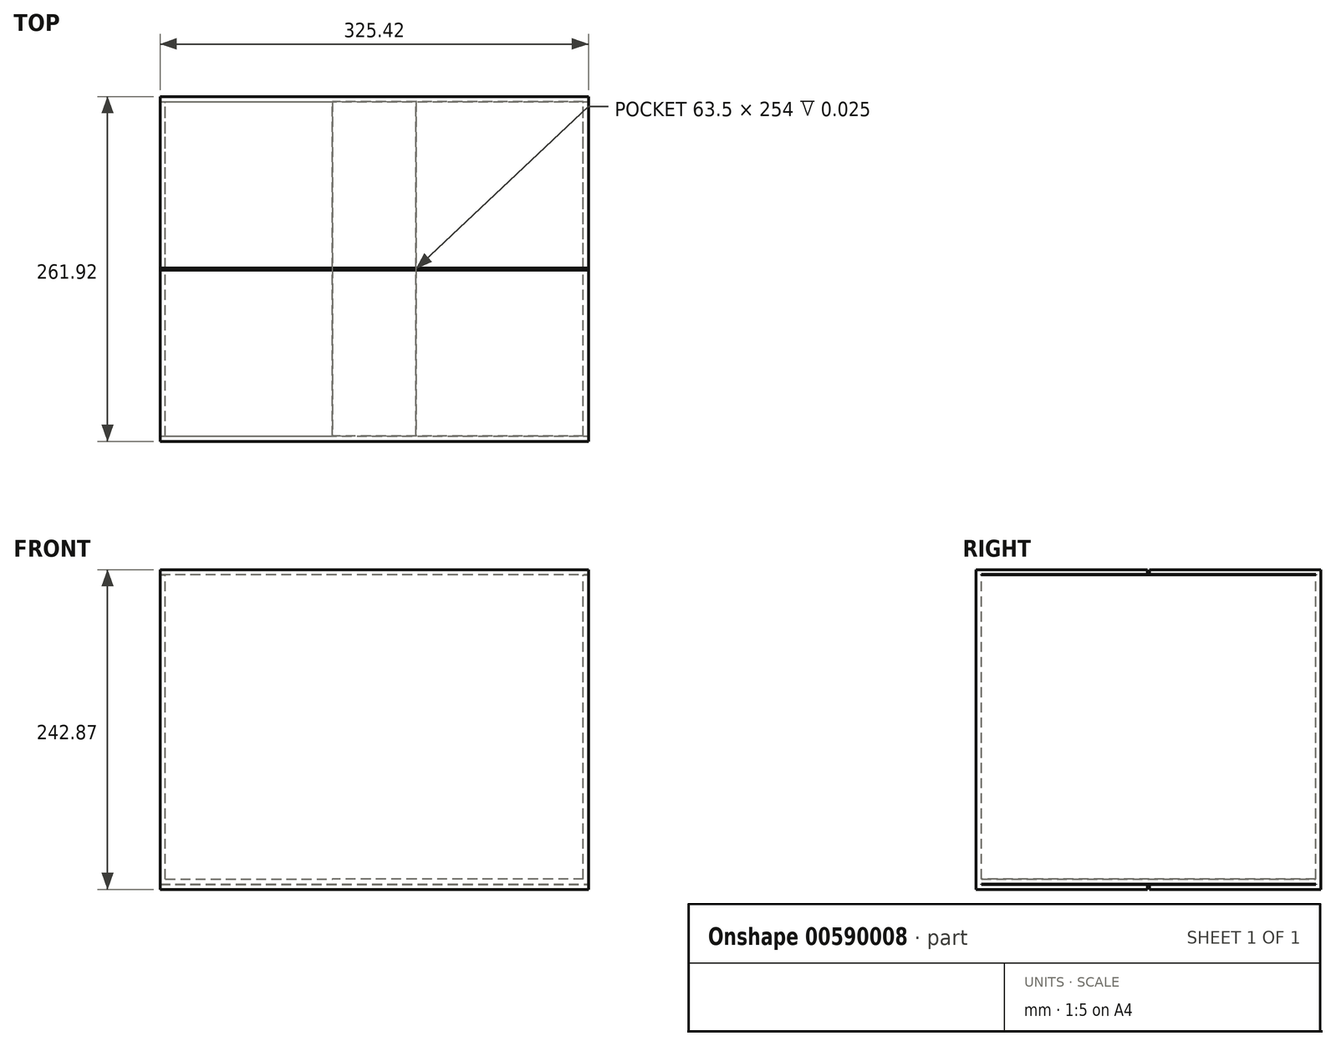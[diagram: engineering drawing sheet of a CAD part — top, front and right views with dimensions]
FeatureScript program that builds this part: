
annotation { "Feature Type Name" : "Feature", "Feature Type Description" : "" }
export const myFeature = defineFeature(function(context is Context, id is Id, definition is map)
    precondition{}
    {
        {
            var Q0;
            Q0=qCreatedBy(makeId("Top.planeOp"),FACE);
            var sketch = newSketch(context, id + "F0", { "sketchPlane" : qUnion([Q0])});
            skLineSegment(sketch, "E0.bottom", {"start": v(162.71, 130.96) * mm, "end": v(-162.71, 130.96) * mm});
            skLineSegment(sketch, "E0.top", {"start": v(162.71, -130.96) * mm, "end": v(-162.71, -130.96) * mm});
            skLineSegment(sketch, "E0.left", {"start": v(162.71, 130.96) * mm, "end": v(162.71, -130.96) * mm});
            skLineSegment(sketch, "E0.right", {"start": v(-162.71, 130.96) * mm, "end": v(-162.71, -130.96) * mm});
            skPoint(sketch, "E0.middle", {"position": v(0, 0) * mm});
            skSolve(sketch);
        }
        {
            var Q0;
            Q0 = qSketchRegion(id + "F0", true);
            extrude(context, id + "F1", {"entities" : qUnion([Q0]), "depth" : 242.87 * mm, "offsetDistance" : 25.4 * mm});
        }
        {
            var Q0;
            Q0=makeQuery(id+"F1.opExtrude","CAP_FACE",FACE,{"disambiguationData":[OSD([sQuery(id+"F0.wireOp",EDGE,"E0.bottom"),sQuery(id+"F0.wireOp",EDGE,"E0.top"),sQuery(id+"F0.wireOp",EDGE,"E0.left"),sQuery(id+"F0.wireOp",EDGE,"E0.right")])],"isStart":false});
            var sketch = newSketch(context, id + "F2", { "sketchPlane" : qUnion([Q0])});
            skLineSegment(sketch, "E1.bottom", {"start": v(158.75, 127) * mm, "end": v(-158.75, 127) * mm});
            skLineSegment(sketch, "E1.top", {"start": v(158.75, -127) * mm, "end": v(-158.75, -127) * mm});
            skLineSegment(sketch, "E1.left", {"start": v(158.75, 127) * mm, "end": v(158.75, -127) * mm});
            skLineSegment(sketch, "E1.right", {"start": v(-158.75, 127) * mm, "end": v(-158.75, -127) * mm});
            skPoint(sketch, "E1.middle", {"position": v(0, 0) * mm});
            skSolve(sketch);
        }
        {
            var Q0;
            Q0 = qSketchRegion(id + "F2", true);
            extrude(context, id + "F3", {"entities" : qUnion([Q0]), "operationType" : NewBodyOperationType.REMOVE, "oppositeDirection" : true, "depth" : 234.95 * mm, "offsetDistance" : 25.4 * mm});
        }
        {
            var Q0;
            Q0=makeQuery(id+"FU8CDPnAfcsiamF_1.boolean.opBoolean","MERGE",FACE,{"derivedFrom":[makeQuery(id+"FkqQ1I0agcOGDgH_1.boolean.opBoolean","MERGE",FACE,{"derivedFrom":[makeQuery(id+"F1.opExtrude","SWEPT_FACE",FACE,{"disambiguationData":[OSD([sQuery(id+"F0.wireOp",EDGE,"E0.left")])]}),makeQuery(id+"FkqQ1I0agcOGDgH_1.opExtrude","CAP_FACE",FACE,{"disambiguationData":[OSD([sQuery(id+"FoDB1Ja4WnMUcBU_1.wireOp",EDGE,"G9ktgCgW-cgai-Fx6D-LfIr-onLoDjvsxL8P"),sQuery(id+"FoDB1Ja4WnMUcBU_1.wireOp",EDGE,"sdlmHgrP-dK7O-7TKQ-vJt8-3tbjKW43ichT"),sQuery(id+"FoDB1Ja4WnMUcBU_1.wireOp",EDGE,"px5y0XHo-arw6-IYJl-GCBX-8e45FcqrlFcx"),sQuery(id+"FoDB1Ja4WnMUcBU_1.wireOp",EDGE,"WPK3Supz-hSMR-a29S-F5kb-zUsID9ybsl2w")])],"isStart":true})]}),makeQuery(id+"FU8CDPnAfcsiamF_1.opExtrude","CAP_FACE",FACE,{"disambiguationData":[OSD([sQuery(id+"Fmsg3vMfZlMDxUX_1.wireOp",EDGE,"k8SHwNhE-juRS-rYz1-FTam-3ZzICyqcjuc2"),sQuery(id+"Fmsg3vMfZlMDxUX_1.wireOp",EDGE,"0DMKhqTQ-7xsP-FRrA-W66T-bKl7aLMX0dlD"),sQuery(id+"Fmsg3vMfZlMDxUX_1.wireOp",EDGE,"qFIxm7PK-wiqi-QzEb-MUsV-y8MnjfuZhfVg"),sQuery(id+"Fmsg3vMfZlMDxUX_1.wireOp",EDGE,"azvGMKYQ-cPQm-AWe1-ROgs-fUFS8ZqJpbH7")])],"isStart":true})]});
            var sketch = newSketch(context, id + "F4", { "sketchPlane" : qUnion([Q0])});
            skLineSegment(sketch, "E2.bottom", {"start": v(0.8, 3.96) * mm, "end": v(-0.8, 3.96) * mm});
            skLineSegment(sketch, "E2.top", {"start": v(0.8, -3.96) * mm, "end": v(-0.8, -3.96) * mm});
            skLineSegment(sketch, "E2.left", {"start": v(0.8, 3.58) * mm, "end": v(0.8, -3.96) * mm});
            skLineSegment(sketch, "E2.right", {"start": v(-0.8, 3.58) * mm, "end": v(-0.8, -3.96) * mm});
            skPoint(sketch, "E2.middle", {"position": v(0, 0) * mm});
            skLineSegment(sketch, "E3.bottom", {"start": v(-0.8, 3.96) * mm, "end": v(-127, 3.96) * mm});
            skLineSegment(sketch, "E3.top", {"start": v(-0.8, 3.58) * mm, "end": v(-127, 3.58) * mm});
            skLineSegment(sketch, "E3.right", {"start": v(-127, 3.96) * mm, "end": v(-127, 3.58) * mm});
            skLineSegment(sketch, "E4", {"start": v(0, 0) * mm, "end": v(0, 24.77) * mm, "construction": true});
            skLineSegment(sketch, "E5.MirrorCS", {"start": v(127, 3.96) * mm, "end": v(127, 3.58) * mm});
            skLineSegment(sketch, "E6.MirrorCS", {"start": v(0.8, 3.96) * mm, "end": v(127, 3.96) * mm});
            skLineSegment(sketch, "E7.MirrorCS", {"start": v(0.8, 3.58) * mm, "end": v(127, 3.58) * mm});
            skSolve(sketch);
        }
        {
            var Q0;
            Q0 = qSketchRegion(id + "F4", true);
            extrude(context, id + "F5", {"entities" : qUnion([Q0]), "operationType" : NewBodyOperationType.REMOVE, "oppositeDirection" : true, "depth" : 698.5 * mm, "offsetDistance" : 25.4 * mm});
        }
        {
            var Q0;
            Q0=makeQuery(id+"F5.boolean.opBoolean","COPY",FACE,{"derivedFrom":makeQuery(id+"F5.opExtrude","SWEPT_FACE",FACE,{"disambiguationData":[OSD([sQuery(id+"F4.wireOp",EDGE,"E3.top")])]})});
            cPlane(context, id + "F6", {"entities" : qUnion([Q0]), "cplaneType" : CPlaneType.OFFSET, "offset" : 0.4 * mm, "width" : 152.4 * mm, "height" : 152.4 * mm});
        }
        {
            var Q0;
            Q0=qCreatedBy(id+"F6.planeOp",FACE);
            var sketch = newSketch(context, id + "F7", { "sketchPlane" : qUnion([Q0])});
            skLineSegment(sketch, "E8.bottom", {"start": v(158.75, -127) * mm, "end": v(31.75, -127) * mm});
            skLineSegment(sketch, "E8.top", {"start": v(158.75, 127) * mm, "end": v(31.75, 127) * mm});
            skLineSegment(sketch, "E8.left", {"start": v(158.75, -127) * mm, "end": v(158.75, 127) * mm});
            skLineSegment(sketch, "E8.right", {"start": v(31.75, -127) * mm, "end": v(31.75, 127) * mm});
            skLineSegment(sketch, "E9", {"start": v(0, 0) * mm, "end": v(0, 25.65) * mm, "construction": true});
            skLineSegment(sketch, "E10.MirrorCS", {"start": v(-158.75, -127) * mm, "end": v(-31.75, -127) * mm});
            skLineSegment(sketch, "E11.MirrorCS", {"start": v(-31.75, -127) * mm, "end": v(-31.75, 127) * mm});
            skLineSegment(sketch, "E12.MirrorCS", {"start": v(-158.75, 127) * mm, "end": v(-31.75, 127) * mm});
            skLineSegment(sketch, "E13.MirrorCS", {"start": v(-158.75, -127) * mm, "end": v(-158.75, 127) * mm});
            skSolve(sketch);
        }
        {
            var Q0;
            Q0 = qSketchRegion(id + "F7", true);
            extrude(context, id + "F8", {"entities" : qUnion([Q0]), "operationType" : NewBodyOperationType.ADD, "depth" : 3.96 * mm, "offsetDistance" : 25.4 * mm});
        }
        {
            var Q0;
            Q0=makeQuery(id+"F1.opExtrude","CAP_FACE",FACE,{"disambiguationData":[OSD([sQuery(id+"F0.wireOp",EDGE,"E0.bottom"),sQuery(id+"F0.wireOp",EDGE,"E0.top"),sQuery(id+"F0.wireOp",EDGE,"E0.left"),sQuery(id+"F0.wireOp",EDGE,"E0.right")])],"isStart":false});
            cPlane(context, id + "F9", {"entities" : qUnion([Q0]), "cplaneType" : CPlaneType.OFFSET, "offset" : 4.32 * mm, "oppositeDirection" : true, "width" : 152.4 * mm, "height" : 152.4 * mm});
        }
        {
            var Q0;
            Q0=makeQuery(id+"F1.opExtrude","CAP_FACE",FACE,{"disambiguationData":[OSD([sQuery(id+"F0.wireOp",EDGE,"E0.bottom"),sQuery(id+"F0.wireOp",EDGE,"E0.top"),sQuery(id+"F0.wireOp",EDGE,"E0.left"),sQuery(id+"F0.wireOp",EDGE,"E0.right")])],"isStart":false});
            var sketch = newSketch(context, id + "F10", { "sketchPlane" : qUnion([Q0])});
            skLineSegment(sketch, "E14.bottom", {"start": v(-162.71, -130.96) * mm, "end": v(162.71, -130.96) * mm});
            skLineSegment(sketch, "E14.top", {"start": v(-162.71, 130.96) * mm, "end": v(162.71, 130.96) * mm});
            skLineSegment(sketch, "E14.left", {"start": v(-162.71, -130.96) * mm, "end": v(-162.71, 130.96) * mm});
            skLineSegment(sketch, "E14.right", {"start": v(162.71, -130.96) * mm, "end": v(162.71, 130.96) * mm});
            skSolve(sketch);
        }
        {
            var Q0;
            Q0 = qSketchRegion(id + "F10", true);
            extrude(context, id + "F11", {"entities" : qUnion([Q0]), "operationType" : NewBodyOperationType.ADD, "oppositeDirection" : true, "depth" : 3.96 * mm, "offsetDistance" : 25.4 * mm});
        }
        {
            var Q0;
            Q0=makeQuery(id+"F1.opExtrude","SWEPT_FACE",FACE,{"disambiguationData":[OSD([sQuery(id+"F0.wireOp",EDGE,"E0.left")])]});
            var sketch = newSketch(context, id + "F12", { "sketchPlane" : qUnion([Q0])});
            skLineSegment(sketch, "E15", {"start": v(-0.8, 242.87) * mm, "end": v(-0.8, 239.3) * mm});
            skLineSegment(sketch, "E16", {"start": v(-0.8, 239.3) * mm, "end": v(-127, 239.3) * mm});
            skLineSegment(sketch, "E17", {"start": v(-127, 239.3) * mm, "end": v(-127, 238.91) * mm});
            skLineSegment(sketch, "E18", {"start": v(-127, 238.91) * mm, "end": v(0, 238.91) * mm});
            skPoint(sketch, "E18.endSnap0", {"position": v(0, 242.87) * mm});
            skLineSegment(sketch, "E19", {"start": v(0, 238.91) * mm, "end": v(0, 242.87) * mm});
            skLineSegment(sketch, "E20", {"start": v(-0.8, 242.87) * mm, "end": v(0, 242.87) * mm});
            skLineSegment(sketch, "E21.MirrorCS", {"start": v(127, 239.3) * mm, "end": v(127, 238.91) * mm});
            skLineSegment(sketch, "E22.MirrorCS", {"start": v(0.8, 242.87) * mm, "end": v(0, 242.87) * mm});
            skLineSegment(sketch, "E23.MirrorCS", {"start": v(0.8, 242.87) * mm, "end": v(0.8, 239.3) * mm});
            skLineSegment(sketch, "E24.MirrorCS", {"start": v(0.8, 239.3) * mm, "end": v(127, 239.3) * mm});
            skLineSegment(sketch, "E25.MirrorCS", {"start": v(127, 238.91) * mm, "end": v(0, 238.91) * mm});
            skSolve(sketch);
        }
        {
            var Q0;
            Q0 = qSketchRegion(id + "F12", true);
            extrude(context, id + "F13", {"entities" : qUnion([Q0]), "operationType" : NewBodyOperationType.REMOVE, "oppositeDirection" : true, "depth" : 338.33 * mm, "offsetDistance" : 25.4 * mm});
        }
    });
